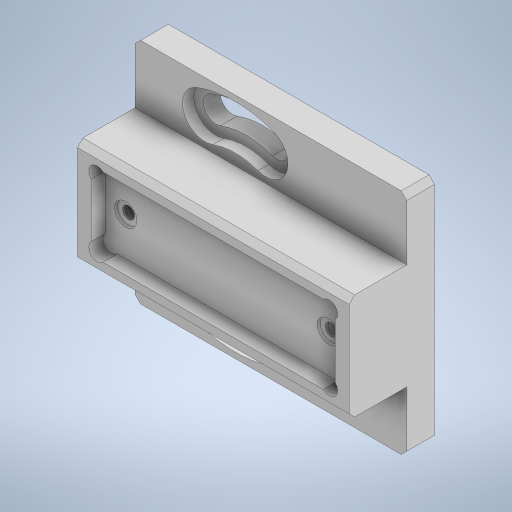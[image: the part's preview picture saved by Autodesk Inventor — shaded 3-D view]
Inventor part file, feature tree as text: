
AUTODESK INVENTOR PART (.ipt)
format: ipt  version: 2024.2 (Build 282272000, 272)  size: 484,864 bytes
history: native  units: in
note: dims shown in document units (in); Inventor stores cm internally (conversion verified against a paired STEP export)
features: extrude x10, hole x6, sketch x4, chamfer x3
ambient origin geometry x8: Origin, YZ Plane, XZ Plane, XY Plane, X Axis, Y Axis, Z Axis, Center Point
bodies: Solid1 (feature_tree)
feature tree (23):
  extrude  "Extrusion1"  TaperAngle=0.0deg  [1 undecoded]
  hole  "Hole1"  [1 undecoded]
  hole  "Hole2"  [1 undecoded]
  hole  "Hole3"  [1 undecoded]
  extrude  "Extrusion2"  TaperAngle=0.0deg  [1 undecoded]
  extrude  "Extrusion3"  Depth=0.0197in
  hole  "Hole5"  [1 undecoded]
  chamfer  "Chamfer2"  [1 undecoded]
  hole  "Hole6"  [1 undecoded]
  extrude  "Extrusion4"  Depth=0.1969in
  extrude  "Extrusion5"  Depth=0.0413in
  extrude  "Extrusion6"  Depth=0.0827in TaperAngle=0.0deg
  chamfer  "Chamfer5"  Distance=1.9213in
  chamfer  "Chamfer6"  Distance=1.6142in
  sketch  "Sketch12"  dims[d2=0.5059in d3=0.0in]
  extrude  "Extrusion12"  Depth=0.1969in TaperAngle=0.0deg
  extrude  "Extrusion13"  TaperAngle=0.0deg  [1 undecoded]
  hole  "Hole7"  [1 undecoded]
  sketch  "Sketch15"  dims[d12=0.0in d13=1.4331in]
  sketch  "Sketch17"  dims[d14=0.7165in d15=0.1772in d16=0.224in d17=0.315in d18=0.3445in d19=0.5635in d20=0.3492in d21=0.0in d22=0.0in d23=0.0in d24=0.0394in d25=0.0in d26=0.0in d27=0.3937in d28=0.1969in d29=0.0413in d30=0.0827in d31=0.224in d32=0.315in d33=0.1654in d34=0.5635in d35=0.0827in d36=0.0in d37=0.0827in d38=0.0in d39=1.9213in d40=1.6142in d41=0.1969in d42=0.0in d54=0.0in d55=0.0in d56=0.0in d57=0.0in d58=0.1575in d59=0.224in d60=0.315in d61=0.0787in d62=0.5635in d63=0.0197in d64=0.0in d68=0.0394in d69=0.0787in d70=45.0deg d77=0.0394in d78=0.0413in d79=0.3937in d80=0.0in d81=0.0in d82=0.1969in d83=0.0827in d84=0.224in d85=0.315in d86=0.0787in d87=0.5635in d88=0.0827in d89=0.0in d90=0.0827in d91=0.0in d92=1.0in d93=0.0in d94=0.4862in d95=0.0in d96=0.0in d97=1.9213in d98=0.748in d99=1.7244in d100=0.5512in d101=0.0984in d102=0.0in d103=0.0394in d104=0.0787in d105=45.0deg d106=0.1181in d107=45.0deg d108=45.0deg d109=45.0deg d110=0.1181in d111=0.1181in d112=0.1181in d113=0.0394in d114=0.0787in d115=45.0deg d118=0.315in d122=0.1772in d129=0.0in d130=0.0in d131=0.0787in d132=0.0in d133=0.0827in d134=0.2362in d135=0.1575in d136=0.0787in d137=90.0deg d138=0.0827in d139=0.0in d140=1.5354in d141=0.9055in d142=1.3976in d143=1.0433in d147=0.315in d148=0.1772in d149=0.1772in d150=0.315in d151=0.0in d152=0.0in d153=0.0787in d154=0.0in d127=0.0197in d128=0.0344in]
  extrude  "Extrusion14"  TaperAngle=0.0deg  [1 undecoded]
  extrude  "Extrusion15"  TaperAngle=0.0deg  [1 undecoded]
  sketch  "Sketch14"  dims[d4=0.0849in d5=0.224in d6=0.1575in d7=0.0787in d8=90.0deg d9=0.3492in d10=0.0in d11=0.0in]
note: 12 required parameter values undecoded (feature->parameter linkage not recoverable at this tier; creation-order binding heuristic only, values carry confidence <= 0.55)
